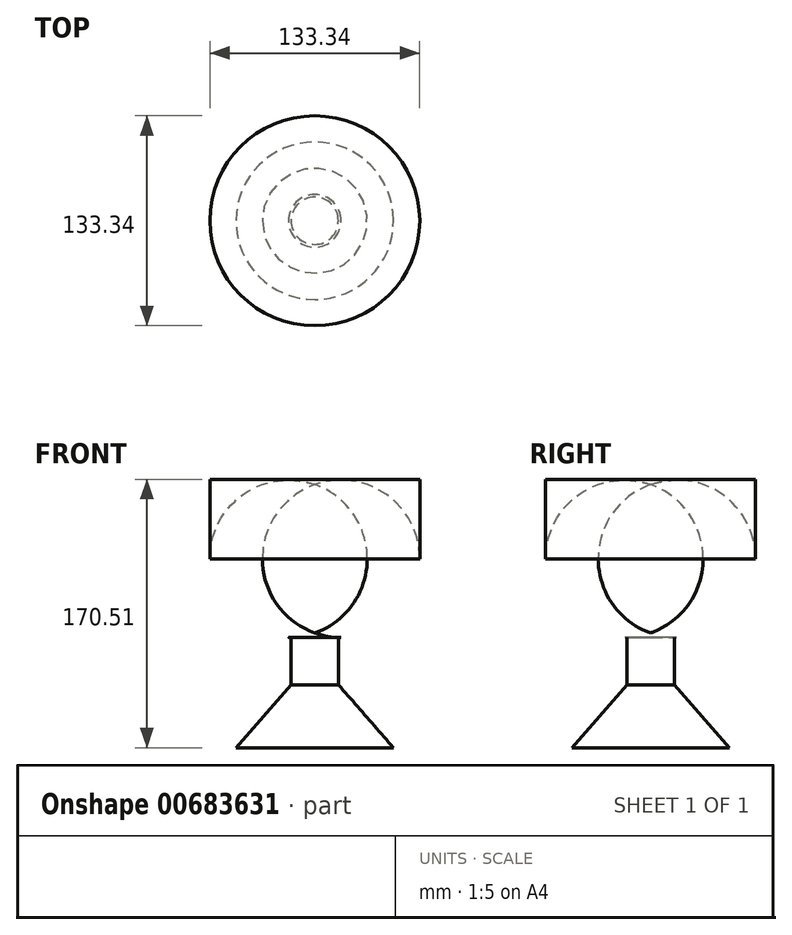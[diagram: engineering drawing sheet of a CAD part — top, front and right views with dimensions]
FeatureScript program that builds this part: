
annotation { "Feature Type Name" : "Feature", "Feature Type Description" : "" }
export const myFeature = defineFeature(function(context is Context, id is Id, definition is map)
    precondition{}
    {
        {
            var Q0;
            Q0=qCreatedBy(makeId("Top.planeOp"),FACE);
            cPlane(context, id + "F0", {"entities" : qUnion([Q0]), "cplaneType" : CPlaneType.OFFSET, "offset" : 70 * mm, "oppositeDirection" : true, "width" : 150 * mm, "height" : 150 * mm});
        }
        {
            var Q0;
            Q0=qCreatedBy(id+"F0.planeOp",FACE);
            var sketch = newSketch(context, id + "F1", { "sketchPlane" : qUnion([Q0])});
            skCircle(sketch, "E0", {"center": v(0, 0) * mm, "radius": 50 * mm});
            skSolve(sketch);
        }
        {
            var Q0;
            Q0=qCreatedBy(makeId("Top.planeOp"),FACE);
            cPlane(context, id + "F2", {"entities" : qUnion([Q0]), "cplaneType" : CPlaneType.OFFSET, "offset" : 30 * mm, "oppositeDirection" : true, "width" : 150 * mm, "height" : 150 * mm});
        }
        {
            var Q0;
            Q0=qCreatedBy(id+"F2.planeOp",FACE);
            var sketch = newSketch(context, id + "F3", { "sketchPlane" : qUnion([Q0])});
            skCircle(sketch, "E1", {"center": v(0, 0) * mm, "radius": 15 * mm});
            skSolve(sketch);
        }
        {
            var Q0;
            Q0=makeQuery(id+"F3.imprint","IMPRINT",FACE,{"disambiguationData":[TD([[makeQuery(id+"F3.imprint","IMPRINT",EDGE,{"derivedFrom":sQuery(id+"F3.wireOp",EDGE,"E1")}),1.0]])]});
            var Q1;
            Q1=makeQuery(id+"F1.imprint","IMPRINT",FACE,{"disambiguationData":[TD([[makeQuery(id+"F1.imprint","IMPRINT",EDGE,{"derivedFrom":sQuery(id+"F1.wireOp",EDGE,"E0")}),1.0]])]});
            loft(context, id + "F4", {"sheetProfilesArray" : [{ "sheetProfileEntities" : qUnion([Q0]) }, { "sheetProfileEntities" : qUnion([Q1]) }]});
        }
        {
            var Q0;
            Q0=qCreatedBy(makeId("Top.planeOp"),FACE);
            cPlane(context, id + "F5", {"entities" : qUnion([Q0]), "cplaneType" : CPlaneType.OFFSET, "offset" : 0 * mm, "oppositeDirection" : true, "width" : 150 * mm, "height" : 150 * mm});
        }
        {
            var Q0;
            Q0=qCreatedBy(id+"F5.planeOp",FACE);
            var sketch = newSketch(context, id + "F6", { "sketchPlane" : qUnion([Q0])});
            skCircle(sketch, "E2", {"center": v(0, 0) * mm, "radius": 15 * mm});
            skSolve(sketch);
        }
        {
            var Q1;
            Q1=makeQuery(id+"F4.opLoft","CAP_FACE",FACE,{"disambiguationData":[OSD([makeQuery(id+"F3.imprint","IMPRINT",FACE,{"disambiguationData":[TD([[makeQuery(id+"F3.imprint","IMPRINT",EDGE,{"derivedFrom":sQuery(id+"F3.wireOp",EDGE,"E1")}),1.0]])]})])],"isStart":true});
            var Q2;
            Q2=makeQuery(id+"F6.imprint","IMPRINT",FACE,{"disambiguationData":[TD([[makeQuery(id+"F6.imprint","IMPRINT",EDGE,{"derivedFrom":sQuery(id+"F6.wireOp",EDGE,"E2")}),1.0]])]});
            loft(context, id + "F7", {"operationType" : NewBodyOperationType.ADD, "sheetProfilesArray" : [{ "sheetProfileEntities" : qUnion([Q1]) }, { "sheetProfileEntities" : qUnion([Q2]) }]});
        }
        {
            var Q0;
            Q0=qCreatedBy(makeId("Front.planeOp"),FACE);
            var sketch = newSketch(context, id + "F8", { "sketchPlane" : qUnion([Q0])});
            skLineSegment(sketch, "E3.bottom", {"start": v(0, 100.5) * mm, "end": v(66.67, 100.5) * mm});
            skLineSegment(sketch, "E3.top", {"start": v(0, 0) * mm, "end": v(16.67, 0) * mm});
            skLineSegment(sketch, "E3.left", {"start": v(0, 100.5) * mm, "end": v(0, 0) * mm});
            skLineSegment(sketch, "E3.right", {"start": v(66.67, 100.5) * mm, "end": v(66.67, 50) * mm});
            skLineSegment(sketch, "E4.MirrorCS", {"start": v(-66.67, 100.5) * mm, "end": v(-66.67, 50) * mm});
            skLineSegment(sketch, "E5.MirrorCS", {"start": v(0, 100.5) * mm, "end": v(-66.67, 100.5) * mm});
            skLineSegment(sketch, "E6.MirrorCS", {"start": v(0, 0) * mm, "end": v(-16.67, 0) * mm});
            skPoint(sketch, "E7.visualSharp", {"position": v(-66.67, 0) * mm});
            skArc(sketch, "E7.filletArc", {"start": v(-66.67, 50) * mm, "mid": v(-52.03, 14.64) * mm, "end": v(-16.67, 0) * mm});
            skPoint(sketch, "E8.visualSharp", {"position": v(66.67, 0) * mm});
            skArc(sketch, "E8.filletArc", {"start": v(16.67, 0) * mm, "mid": v(52.03, 14.64) * mm, "end": v(66.67, 50) * mm});
            skSolve(sketch);
        }
        {
            var Q0;
            Q0=makeQuery(id+"F8.imprint","IMPRINT",FACE,{"disambiguationData":[TD([[makeQuery(id+"F8.imprint","IMPRINT",EDGE,{"derivedFrom":sQuery(id+"F8.wireOp",EDGE,"E3.left")}),-1.0]])]});
            var Q1;
            Q1=sQuery(id+"F8.wireOp",EDGE,"E3.left");
            revolve(context, id + "F9", {"operationType" : NewBodyOperationType.ADD, "entities" : qUnion([Q0]), "axis" : qUnion([Q1]), "revolveType" : RevolveType.FULL});
        }
    });
